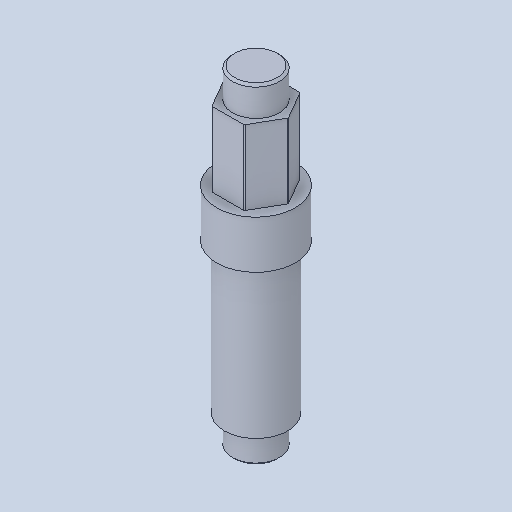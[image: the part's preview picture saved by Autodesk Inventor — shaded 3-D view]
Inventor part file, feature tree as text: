
AUTODESK INVENTOR PART (.ipt)
format: ipt  version: 2023.4 (Build 274418000, 418)  size: 114,688 bytes
history: native  units: in
note: dims shown in document units (in); Inventor stores cm internally (conversion verified against a paired STEP export)
features: chamfer x1
ambient origin geometry x8: Origin, YZ Plane, XZ Plane, XY Plane, X Axis, Y Axis, Z Axis, Center Point
bodies: Solid1 (feature_tree)
feature tree (1):
  chamfer  "Chamfer1"  [1 undecoded]
note: 1 required parameter value undecoded (feature->parameter linkage not recoverable at this tier; creation-order binding heuristic only, values carry confidence <= 0.55)
